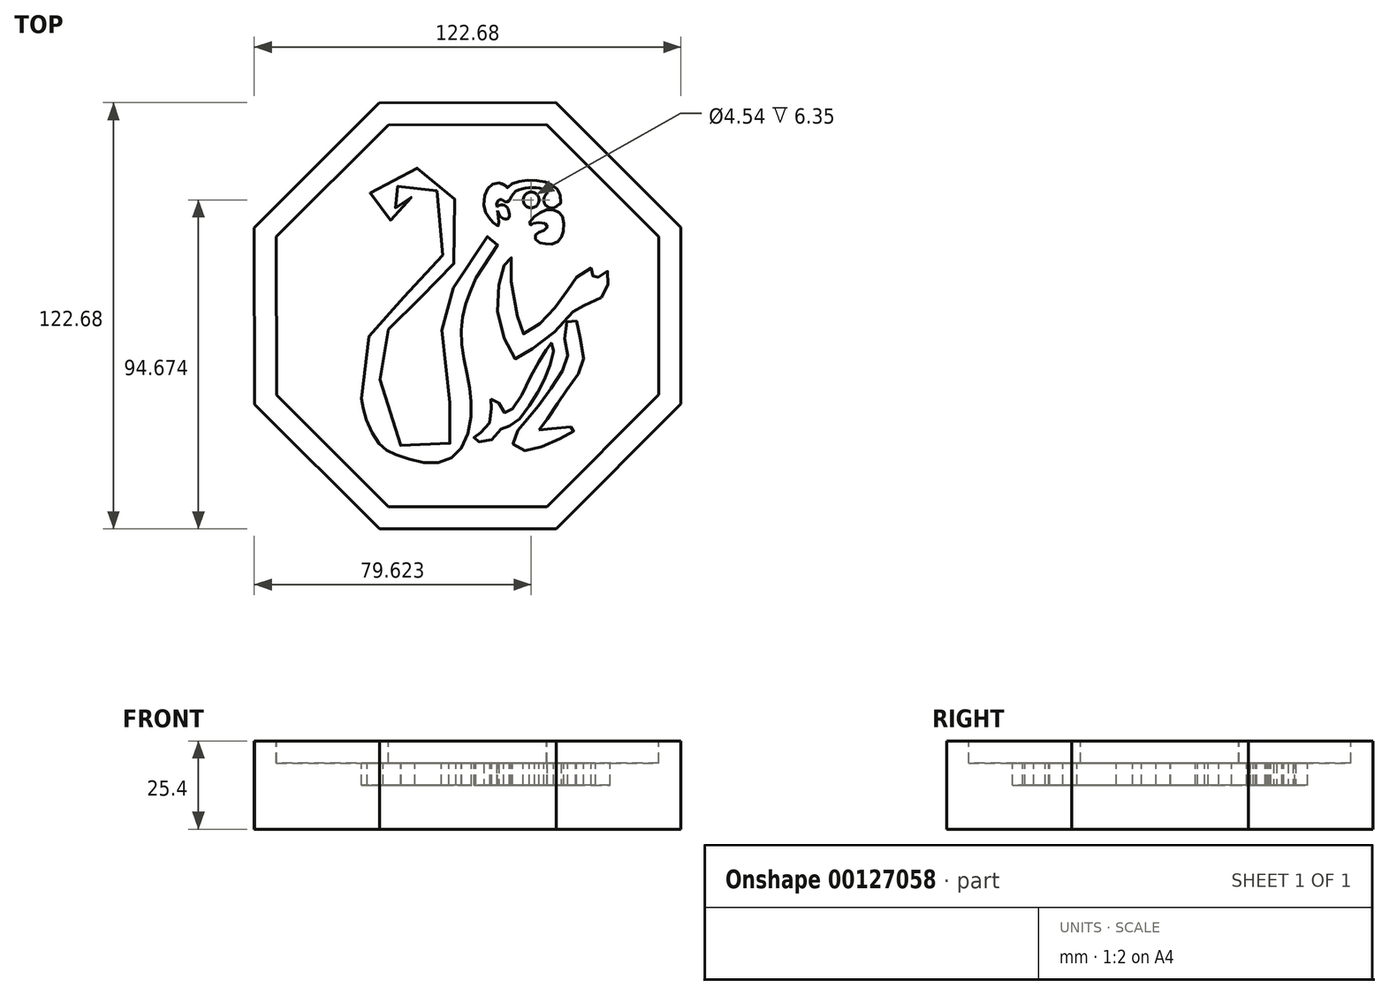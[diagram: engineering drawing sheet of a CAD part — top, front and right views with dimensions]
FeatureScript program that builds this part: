
annotation { "Feature Type Name" : "Feature", "Feature Type Description" : "" }
export const myFeature = defineFeature(function(context is Context, id is Id, definition is map)
    precondition{}
    {
        {
            var Q0;
            Q0=qCreatedBy(makeId("Top.planeOp"),FACE);
            var sketch = newSketch(context, id + "F0", { "sketchPlane" : qUnion([Q0])});
            skCircle(sketch, "E0.cCircle", {"center": v(0, 0) * mm, "radius": 61.32 * mm, "construction": true});
            skLineSegment(sketch, "E0.0", {"start": v(-61.3, -25.44) * mm, "end": v(-61.34, 25.36) * mm});
            skLineSegment(sketch, "E0.1", {"start": v(-61.34, 25.36) * mm, "end": v(-25.44, 61.3) * mm});
            skLineSegment(sketch, "E0.2", {"start": v(-25.44, 61.3) * mm, "end": v(25.36, 61.34) * mm});
            skLineSegment(sketch, "E0.3", {"start": v(25.36, 61.34) * mm, "end": v(61.3, 25.44) * mm});
            skLineSegment(sketch, "E0.4", {"start": v(61.3, 25.44) * mm, "end": v(61.34, -25.36) * mm});
            skLineSegment(sketch, "E0.5", {"start": v(61.34, -25.36) * mm, "end": v(25.44, -61.3) * mm});
            skLineSegment(sketch, "E0.6", {"start": v(25.44, -61.3) * mm, "end": v(-25.36, -61.34) * mm});
            skLineSegment(sketch, "E0.7", {"start": v(-25.36, -61.34) * mm, "end": v(-61.3, -25.44) * mm});
            skPoint(sketch, "E0.0.midPoint", {"position": v(-61.32, -0.04) * mm});
            skSolve(sketch);
        }
        {
            var Q0;
            Q0=qSketchRegion(id+"F0",true);
            extrude(context, id + "F1", {"entities" : qUnion([Q0]), "depth" : 25.4 * mm});
        }
        {
            var Q0;
            Q0=makeQuery(id+"F1.opExtrude","CAP_FACE",FACE,{"disambiguationData":[OSD([sQuery(id+"F0.wireOp",EDGE,"E0.0"),sQuery(id+"F0.wireOp",EDGE,"E0.1"),sQuery(id+"F0.wireOp",EDGE,"E0.2"),sQuery(id+"F0.wireOp",EDGE,"E0.3"),sQuery(id+"F0.wireOp",EDGE,"E0.4"),sQuery(id+"F0.wireOp",EDGE,"E0.5"),sQuery(id+"F0.wireOp",EDGE,"E0.6"),sQuery(id+"F0.wireOp",EDGE,"E0.7")])],"isStart":false});
            var sketch = newSketch(context, id + "F2", { "sketchPlane" : qUnion([Q0])});
            skLineSegment(sketch, "E1.0", {"start": v(-54.96, -22.8) * mm, "end": v(-54.99, 22.73) * mm});
            skLineSegment(sketch, "E1.1", {"start": v(-22.73, -54.99) * mm, "end": v(-54.96, -22.8) * mm});
            skLineSegment(sketch, "E1.2", {"start": v(-54.99, 22.73) * mm, "end": v(-22.8, 54.96) * mm});
            skLineSegment(sketch, "E1.3", {"start": v(22.8, -54.96) * mm, "end": v(-22.73, -54.99) * mm});
            skLineSegment(sketch, "E1.4", {"start": v(-22.8, 54.96) * mm, "end": v(22.73, 54.99) * mm});
            skLineSegment(sketch, "E1.5", {"start": v(22.73, 54.99) * mm, "end": v(54.96, 22.8) * mm});
            skLineSegment(sketch, "E1.6", {"start": v(54.96, 22.8) * mm, "end": v(54.99, -22.73) * mm});
            skLineSegment(sketch, "E1.7", {"start": v(54.99, -22.73) * mm, "end": v(22.8, -54.96) * mm});
            skSolve(sketch);
        }
        {
            var Q0;
            Q0=qSketchRegion(id+"F2",true);
            extrude(context, id + "F3", {"entities" : qUnion([Q0]), "operationType" : NewBodyOperationType.REMOVE, "oppositeDirection" : true, "depth" : 6.35 * mm});
        }
        {
            var Q0;
            Q0=makeQuery(id+"F3.boolean.opBoolean","COPY",FACE,{"derivedFrom":makeQuery(id+"F3.opExtrude","CAP_FACE",FACE,{"disambiguationData":[OSD([sQuery(id+"F2.wireOp",EDGE,"E1.0"),sQuery(id+"F2.wireOp",EDGE,"E1.1"),sQuery(id+"F2.wireOp",EDGE,"E1.2"),sQuery(id+"F2.wireOp",EDGE,"E1.3"),sQuery(id+"F2.wireOp",EDGE,"E1.4"),sQuery(id+"F2.wireOp",EDGE,"E1.5"),sQuery(id+"F2.wireOp",EDGE,"E1.6"),sQuery(id+"F2.wireOp",EDGE,"E1.7")])],"isStart":false})});
            var sketch = newSketch(context, id + "F4", { "sketchPlane" : qUnion([Q0])});
            skFitSpline(sketch, "E2", {"points": [v(2.44, 10.87) * mm, v(4.53, 14.3) * mm, v(7.22, 17.73) * mm, v(9.18, 21.28) * mm, v(10.4, 23.24) * mm, v(9.79, 24.83) * mm, v(6.12, 23.11) * mm, v(-1.72, 14.06) * mm, v(-4.53, 6.6) * mm, v(-6.55, 1.32) * mm, v(-7.35, -2.59) * mm, v(-6.98, -14.58) * mm, v(-4.29, -27.8) * mm, v(-3.3, -31.35) * mm, v(-4.35, -35.63) * mm, v(-8.45, -39.06) * mm, v(-16.53, -38.45) * mm, v(-23.87, -32.45) * mm, v(-25.22, -16.3) * mm, v(-25.22, -11.03) * mm, v(-22.5, -3.59) * mm, v(-18.8, 0) * mm, v(-14.71, 4.07) * mm, v(-10.94, 7.43) * mm, v(-7.56, 10.59) * mm, v(-2.08, 19.07) * mm, v(-3.06, 31.68) * mm, v(-6.03, 37.52) * mm, v(-11.92, 42) * mm, v(-19.55, 41.67) * mm, v(-26.75, 36.98) * mm, v(-28.82, 32.29) * mm, v(-26.53, 28.58) * mm, v(-21.63, 27.5) * mm, v(-16.5, 28.58) * mm, v(-15.2, 31.52) * mm, v(-17.37, 35.34) * mm, v(-19.12, 35.34) * mm, v(-19.12, 33.6) * mm, v(-19.77, 31.52) * mm, v(-23.26, 31.42) * mm, v(-24.13, 34.47) * mm, v(-21.3, 36.87) * mm, v(-15.96, 38.29) * mm, v(-11.92, 38.61) * mm, v(-7.67, 33.92) * mm, v(-5.7, 21.38) * mm, v(-11.38, 11.9) * mm, v(-17.15, 6.23) * mm, v(-21.84, 2.96) * mm, v(-27.08, -2.93) * mm, v(-30.13, -14.7) * mm, v(-30.46, -23.87) * mm], "startDerivative": vector(121.12, 223.82) * mm, "endDerivative": vector(1.74, -365.53) * mm});
            skFitSpline(sketch, "E3", {"points": [v(-30.46, -23.87) * mm, v(-29.34, -29.18) * mm, v(-25.26, -37) * mm, v(-21.17, -39.67) * mm, v(-11.6, -42.29) * mm, v(-2.8, -39.4) * mm, v(1.03, -27.72) * mm, v(0, -17.8) * mm, v(-1.74, -6.82) * mm, v(-0.9, 1.99) * mm, v(2.44, 10.87) * mm], "startDerivative": vector(10.43, -61.5) * mm, "endDerivative": vector(36.7, 83.52) * mm});
            skFitSpline(sketch, "E4", {"points": [v(6.65, -23.99) * mm, v(8.2, -24.17) * mm, v(10.5, -27.8) * mm, v(10.96, -27.8) * mm, v(13.16, -26.65) * mm, v(17.29, -19.22) * mm, v(20.95, -12.44) * mm, v(23.06, -9.04) * mm, v(24.07, -7.85) * mm, v(24.71, -8.68) * mm, v(24.16, -12.53) * mm, v(22.05, -18.3) * mm, v(19.58, -22.89) * mm, v(15.91, -28.48) * mm, v(12.43, -31.7) * mm, v(10.4, -31.87) * mm, v(7.75, -35.08) * mm, v(3.44, -36.27) * mm, v(1.97, -35.82) * mm, v(1.97, -34.72) * mm, v(3.62, -33.7) * mm, v(6.56, -30.31) * mm, v(6.65, -25.55) * mm, v(6.65, -23.99) * mm]});
            skFitSpline(sketch, "E5", {"points": [v(20.59, -32.8) * mm, v(22.42, -30.4) * mm, v(26, -25.09) * mm, v(28.84, -20.96) * mm, v(32.7, -15) * mm, v(33.24, -10.14) * mm, v(31.31, -2.07) * mm, v(31.13, -1.16) * mm, v(28.38, -1.9) * mm, v(28.1, -7.4) * mm, v(28.75, -12.25) * mm, v(26.18, -17.48) * mm, v(21.32, -24.81) * mm, v(17.47, -29.4) * mm, v(14.81, -32.6) * mm, v(12.98, -36.37) * mm, v(15.27, -38.57) * mm, v(20.04, -38.1) * mm, v(26.55, -35.36) * mm, v(30.58, -33.16) * mm, v(31.04, -32.42) * mm, v(28.75, -31.97) * mm, v(21.96, -32.88) * mm, v(20.59, -32.8) * mm]});
            skFitSpline(sketch, "E6", {"points": [v(10.55, 14.56) * mm, v(11.09, 16.4) * mm, v(12.4, 16.95) * mm, v(12.47, 15.1) * mm, v(13.01, 5.61) * mm, v(15.17, -3.56) * mm, v(15.87, -5.18) * mm, v(18.18, -4.18) * mm, v(21.88, -1.33) * mm, v(25.04, 2.22) * mm, v(28.13, 6.54) * mm, v(29.36, 8.31) * mm, v(30.36, 10.09) * mm, v(33.9, 12.86) * mm, v(35.3, 13.63) * mm, v(36.3, 13.94) * mm, v(36.76, 12.86) * mm, v(35.68, 10.93) * mm, v(35.68, 10.24) * mm, v(37, 10.93) * mm, v(38.92, 11.78) * mm, v(39.3, 12.86) * mm, v(40.85, 12.48) * mm, v(40.54, 10.78) * mm, v(40.23, 8.08) * mm, v(39.46, 6.08) * mm, v(37.38, 4.61) * mm, v(33.99, 3) * mm, v(31.6, 3.07) * mm, v(31.2, 2.37) * mm, v(26.58, -2.95) * mm, v(22.5, -6.95) * mm, v(15.33, -11.58) * mm, v(13.78, -12.44) * mm, v(11.7, -9.27) * mm, v(9.08, -1.9) * mm, v(8.54, 4.84) * mm, v(9.47, 11.09) * mm, v(10.55, 14.56) * mm]});
            skCircle(sketch, "E7", {"center": v(18.28, 33.33) * mm, "radius": 2.27 * mm});
            skCircle(sketch, "E8", {"center": v(24.21, 33.33) * mm, "radius": 2.3 * mm});
            skFitSpline(sketch, "E9", {"points": [v(22.82, 35.16) * mm, v(22.7, 35.89) * mm, v(21.23, 36.58) * mm, v(18.98, 36.88) * mm, v(16.08, 36.62) * mm, v(13.91, 35.89) * mm, v(12.53, 34.24) * mm, v(12, 33.16) * mm, v(11.06, 32.73) * mm, v(10.32, 33.12) * mm, v(9.63, 33.55) * mm, v(8.6, 32.86) * mm, v(8.5, 30.65) * mm, v(8.85, 28.14) * mm, v(8.98, 26.89) * mm, v(8.9, 25.9) * mm, v(7.6, 26.63) * mm, v(6.21, 28.23) * mm, v(5, 30.22) * mm, v(4.87, 34.37) * mm, v(6.34, 37.27) * mm, v(8.29, 38.27) * mm, v(10.67, 37.62) * mm, v(11.45, 36.88) * mm, v(12.05, 37.45) * mm, v(14.3, 38.57) * mm, v(18.41, 39) * mm, v(22.57, 38.44) * mm, v(25, 37.14) * mm, v(26.46, 35.32) * mm, v(26.76, 32.25) * mm, v(25.79, 31.67) * mm], "startDerivative": vector(3.45, 41.12) * mm, "endDerivative": vector(-57.96, -0.91) * mm});
            skFitSpline(sketch, "E10", {"points": [v(9.67, 28.4) * mm, v(11.1, 27.84) * mm, v(11.97, 28.44) * mm, v(11.88, 29.92) * mm, v(11.1, 31.52) * mm, v(9.67, 31.95) * mm, v(8.42, 31.28) * mm, v(9.02, 29.27) * mm, v(9.67, 28.4) * mm]});
            skFitSpline(sketch, "E11", {"points": [v(18.85, 26.63) * mm, v(21.18, 26.76) * mm, v(22.83, 26.15) * mm, v(22.61, 24.98) * mm, v(21, 24.25) * mm, v(19.88, 23.55) * mm, v(19.32, 22.69) * mm, v(20.45, 21.17) * mm, v(22.4, 20.74) * mm, v(24.95, 20.79) * mm, v(26.9, 22.43) * mm, v(27.54, 24.42) * mm, v(27.37, 28.1) * mm, v(26.29, 29.74) * mm, v(24, 30.6) * mm, v(21.1, 29.83) * mm, v(18.46, 27.84) * mm, v(17.76, 26.37) * mm, v(18.46, 26.15) * mm, v(18.85, 26.63) * mm]});
            skSolve(sketch);
        }
        {
            var Q0;
            Q0 = qSketchRegion(id + "F4", true);
            extrude(context, id + "F5", {"entities" : qUnion([Q0]), "operationType" : NewBodyOperationType.REMOVE, "oppositeDirection" : true, "depth" : 6.35 * mm});
        }
    });
